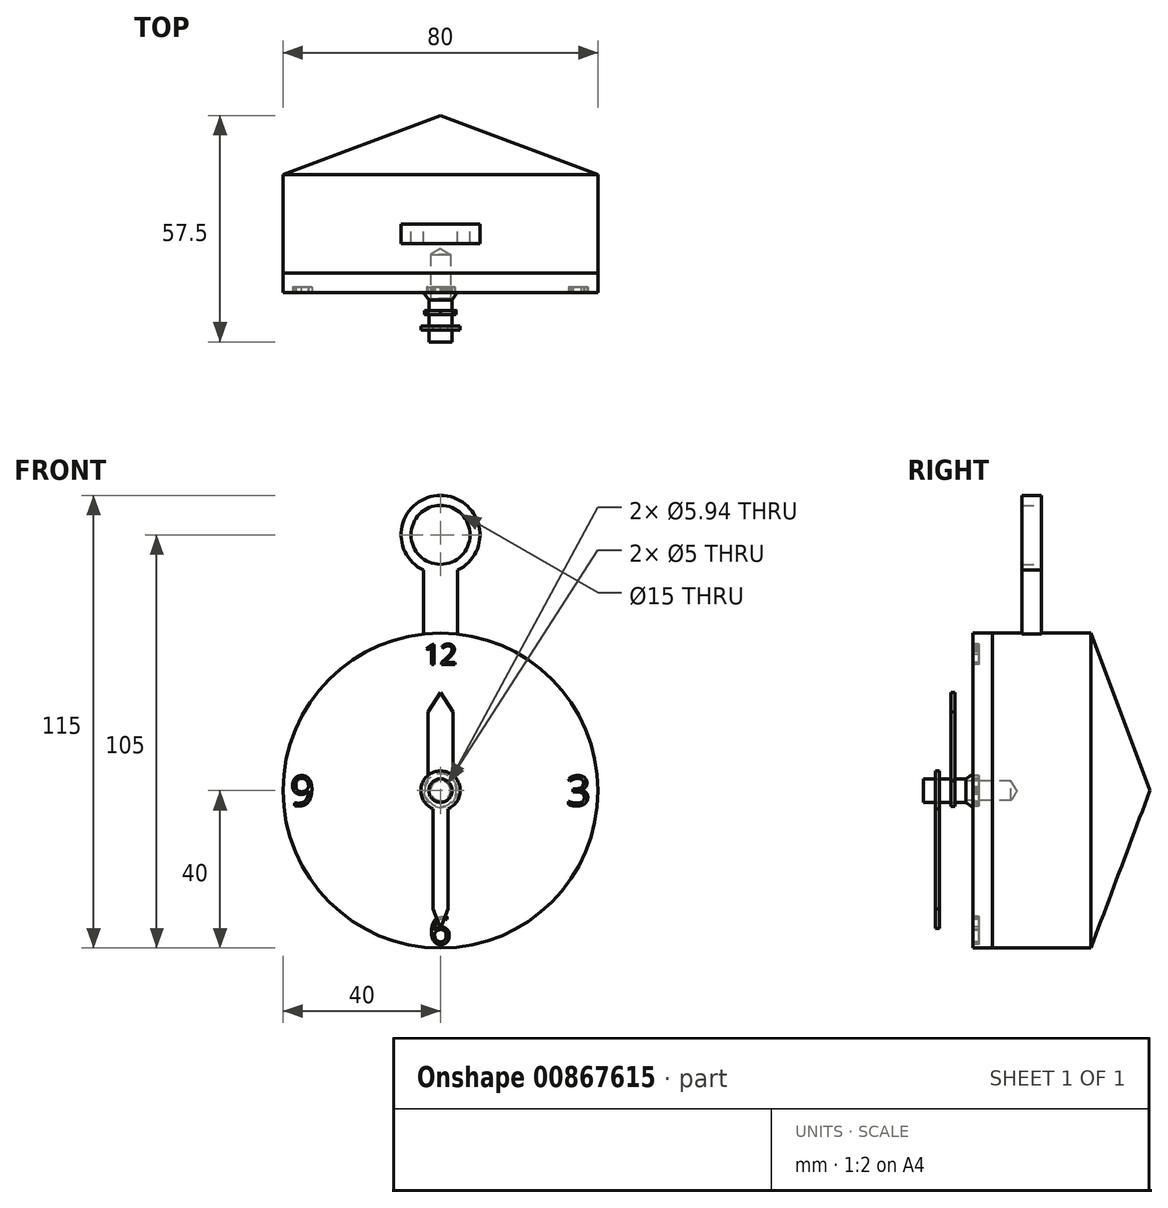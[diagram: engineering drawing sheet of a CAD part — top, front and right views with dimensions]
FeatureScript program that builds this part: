
annotation { "Feature Type Name" : "Feature", "Feature Type Description" : "" }
export const myFeature = defineFeature(function(context is Context, id is Id, definition is map)
    precondition{}
    {
        {
            var Q0;
            Q0=qCreatedBy(makeId("Front.planeOp"),FACE);
            var sketch = newSketch(context, id + "F0", { "sketchPlane" : qUnion([Q0])});
            skCircle(sketch, "E0", {"center": v(0, 0) * mm, "radius": 40 * mm});
            skSolve(sketch);
        }
        {
            var Q0;
            Q0=makeQuery(id+"F0.imprint","IMPRINT",FACE,{"disambiguationData":[TD([[makeQuery(id+"F0.imprint","IMPRINT",EDGE,{"derivedFrom":sQuery(id+"F0.wireOp",EDGE,"E0")}),1.0]])]});
            extrude(context, id + "F1", {"entities" : qUnion([Q0]), "endBound" : BoundingType.SYMMETRIC, "depth" : 25 * mm, "offsetDistance" : 25 * mm});
        }
        {
            var Q0;
            Q0=makeQuery(id+"F1.opExtrude","CAP_FACE",FACE,{"disambiguationData":[OSD([sQuery(id+"F0.wireOp",EDGE,"E0")])],"isStart":true});
            var sketch = newSketch(context, id + "F2", { "sketchPlane" : qUnion([Q0])});
            skSolve(sketch);
        }
        {
            var Q0;
            Q0=makeQuery(id+"F2.imprint","IMPRINT",FACE,{"disambiguationData":[TD([[makeQuery(id+"F2.imprint","IMPRINT",EDGE,{"derivedFrom":makeQuery(id+"F1.opExtrude","CAP_EDGE",EDGE,{"disambiguationData":[OSD([sQuery(id+"F0.wireOp",EDGE,"E0")])],"isStart":true})}),-1.0]])]});
            cPlane(context, id + "F3", {"entities" : qUnion([Q0]), "cplaneType" : CPlaneType.OFFSET, "offset" : 15 * mm, "width" : 150 * mm, "height" : 150 * mm});
        }
        {
            var Q0;
            Q0=qCreatedBy(id+"F3.planeOp",FACE);
            var sketch = newSketch(context, id + "F4", { "sketchPlane" : qUnion([Q0])});
            skPoint(sketch, "E1", {"position": v(0, 0) * mm});
            skSolve(sketch);
        }
        {
            var Q0;
            Q0=sQuery(id+"FzRARXqQxgSWfqW_1.wireOp",EDGE,"R4HBZe7h-dPAi-faUW-LI31-kF577Gu9LWN3");
            var Q1;
            Q1=sQuery(id+"FHscHiDwKJqEqJl_1.wireOp",EDGE,"caf13c96-3b14-45e5-a936-a351d3d8df380.MirrorCS");
            var Q2;
            Q2=sQuery(id+"FzRARXqQxgSWfqW_1.wireOp",EDGE,"7aed7209-74bc-49f3-b477-968225ddfcb50.MirrorCS");
            var Q3;
            Q3=sQuery(id+"FHscHiDwKJqEqJl_1.wireOp",EDGE,"4JvzB8gR-oUBM-6mn4-xHmX-QHIRwTSJfbtS");
            var Q5;
            Q5=makeQuery(id+"F2.imprint","IMPRINT",FACE,{"disambiguationData":[TD([[makeQuery(id+"F2.imprint","IMPRINT",EDGE,{"derivedFrom":makeQuery(id+"F1.opExtrude","CAP_EDGE",EDGE,{"disambiguationData":[OSD([sQuery(id+"F0.wireOp",EDGE,"E0")])],"isStart":true})}),-1.0]])]});
            var Q6;
            Q6=sQuery(id+"F4.wireOp",VERTEX,"E1");
            var Q7;
            Q7=sQuery(id+"FzRARXqQxgSWfqW_1.wireOp",EDGE,"R4HBZe7h-dPAi-faUW-LI31-kF577Gu9LWN3");
            var Q8;
            Q8=sQuery(id+"FHscHiDwKJqEqJl_1.wireOp",EDGE,"caf13c96-3b14-45e5-a936-a351d3d8df380.MirrorCS");
            var Q9;
            Q9=sQuery(id+"FzRARXqQxgSWfqW_1.wireOp",EDGE,"7aed7209-74bc-49f3-b477-968225ddfcb50.MirrorCS");
            var Q10;
            Q10=sQuery(id+"FHscHiDwKJqEqJl_1.wireOp",EDGE,"4JvzB8gR-oUBM-6mn4-xHmX-QHIRwTSJfbtS");
            loft(context, id + "F5", {"operationType" : NewBodyOperationType.ADD, "spine" : qUnion([Q0, Q1, Q2, Q3]), "sheetProfilesArray" : [{ "sheetProfileEntities" : qUnion([Q5]) }, { "sheetProfileEntities" : qUnion([Q6]) }], "guidesArray" : [{ "guideEntities" : qUnion([Q7]), "guideDerivativeType" : LoftGuideDerivativeType.DEFAULT, "guideDerivativeMagnitude" : 1 }, { "guideEntities" : qUnion([Q8]), "guideDerivativeType" : LoftGuideDerivativeType.DEFAULT, "guideDerivativeMagnitude" : 1 }, { "guideEntities" : qUnion([Q9]), "guideDerivativeType" : LoftGuideDerivativeType.DEFAULT, "guideDerivativeMagnitude" : 1 }, { "guideEntities" : qUnion([Q10]), "guideDerivativeType" : LoftGuideDerivativeType.DEFAULT, "guideDerivativeMagnitude" : 1 }]});
        }
        {
            var Q0;
            Q0=makeQuery(id+"F1.opExtrude","CAP_FACE",FACE,{"disambiguationData":[OSD([sQuery(id+"F0.wireOp",EDGE,"E0")])],"isStart":false});
            var sketch = newSketch(context, id + "F6", { "sketchPlane" : qUnion([Q0])});
            skCircle(sketch, "E2", {"center": v(0, 0) * mm, "radius": 40 * mm});
            skSolve(sketch);
        }
        {
            var Q0;
            Q0 = qSketchRegion(id + "F6", true);
            extrude(context, id + "F7", {"entities" : qUnion([Q0]), "depth" : 5 * mm, "offsetDistance" : 25 * mm});
        }
        {
            var Q0;
            Q0=makeQuery(id+"F7.opExtrude","CAP_FACE",FACE,{"disambiguationData":[OSD([sQuery(id+"F6.wireOp",EDGE,"E2")])],"isStart":false});
            var sketch = newSketch(context, id + "F8", { "sketchPlane" : qUnion([Q0])});
            skCircle(sketch, "E3", {"center": v(0, 0) * mm, "radius": 4.25 * mm});
            skSolve(sketch);
        }
        {
            var Q0;
            Q0=makeQuery(id+"F8.imprint","IMPRINT",FACE,{"disambiguationData":[TD([[makeQuery(id+"F8.imprint","IMPRINT",EDGE,{"derivedFrom":sQuery(id+"F8.wireOp",EDGE,"E3")}),-1.0]])]});
            cPlane(context, id + "F9", {"entities" : qUnion([Q0]), "cplaneType" : CPlaneType.OFFSET, "offset" : 2.25 * mm, "width" : 150 * mm, "height" : 150 * mm});
        }
        {
            var Q0;
            Q0=qCreatedBy(id+"F9.planeOp",FACE);
            var sketch = newSketch(context, id + "F10", { "sketchPlane" : qUnion([Q0])});
            skCircle(sketch, "E4.0", {"center": v(0, 0) * mm, "radius": 2.65 * mm});
            skSolve(sketch);
        }
        {
            var Q1;
            Q1=makeQuery(id+"F8.imprint","IMPRINT",FACE,{"disambiguationData":[TD([[makeQuery(id+"F8.imprint","IMPRINT",EDGE,{"derivedFrom":sQuery(id+"F8.wireOp",EDGE,"E3")}),1.0]])]});
            var Q2;
            Q2=makeQuery(id+"F10.imprint","IMPRINT",FACE,{"disambiguationData":[TD([[makeQuery(id+"F10.imprint","IMPRINT",EDGE,{"derivedFrom":sQuery(id+"F10.wireOp",EDGE,"E4.0")}),1.0]])]});
            loft(context, id + "F11", {"operationType" : NewBodyOperationType.ADD, "sheetProfilesArray" : [{ "sheetProfileEntities" : qUnion([Q1]) }, { "sheetProfileEntities" : qUnion([Q2]) }]});
        }
        {
            var Q0;
            Q0=qCreatedBy(id+"F9.planeOp",FACE);
            cPlane(context, id + "F12", {"entities" : qUnion([Q0]), "cplaneType" : CPlaneType.OFFSET, "offset" : 0 * mm, "width" : 150 * mm, "height" : 150 * mm});
        }
        {
            var Q0;
            Q0=qCreatedBy(id+"F12.planeOp",FACE);
            var sketch = newSketch(context, id + "F13", { "sketchPlane" : qUnion([Q0])});
            skPoint(sketch, "E5", {"position": v(0, 0) * mm});
            skSolve(sketch);
        }
        {
            var Q0;
            Q0=sQuery(id+"F13.wireOp",VERTEX,"E5");
            var Q1;
            Q1=makeQuery(id+"F1.opExtrude","SWEPT_BODY",BODY,{"disambiguationData":[OSD([sQuery(id+"F0.wireOp",EDGE,"E0")])]});
            var Q2;
            Q2=makeQuery(id+"F7.opExtrude","SWEPT_BODY",BODY,{"disambiguationData":[OSD([sQuery(id+"F6.wireOp",EDGE,"E2")])]});
            var Q3;
            Q3=makeQuery(id+"F11.opLoft","SWEPT_BODY",BODY,{"disambiguationData":[OSD([makeQuery(id+"F8.imprint","IMPRINT",FACE,{"disambiguationData":[TD([[makeQuery(id+"F8.imprint","IMPRINT",EDGE,{"derivedFrom":sQuery(id+"F8.wireOp",EDGE,"E3")}),1.0]])]}),makeQuery(id+"F10.imprint","IMPRINT",FACE,{"disambiguationData":[TD([[makeQuery(id+"F10.imprint","IMPRINT",EDGE,{"derivedFrom":sQuery(id+"F10.wireOp",EDGE,"E4.0")}),1.0]])]})])]});
            hole(context, id + "F14", {"style" : HoleStyle.C_SINK, "endStyle" : HoleEndStyle.BLIND, "holeDiameter" : 5 * mm, "cSinkDiameter" : 7.5 * mm, "cSinkAngle" : 120 * degree, "majorDiameter" : 5 * mm, "holeDepth" : 12 * mm, "isTappedThrough" : true, "tappedDepth" : 12 * mm, "tapClearance" : 3, "startFromSketch" : true, "locations" : qUnion([Q0]), "scope" : qUnion([Q1, Q2, Q3])});
        }
        {
            var Q0;
            Q0=makeQuery(id+"F7.opExtrude","CAP_FACE",FACE,{"disambiguationData":[OSD([sQuery(id+"F6.wireOp",EDGE,"E2")])],"isStart":false});
            var sketch = newSketch(context, id + "F15", { "sketchPlane" : qUnion([Q0])});
            skCircle(sketch, "E6.0", {"center": v(0, 0) * mm, "radius": 2.97 * mm});
            skSolve(sketch);
        }
        {
            var Q0;
            Q0 = qSketchRegion(id + "F15", true);
            extrude(context, id + "F16", {"entities" : qUnion([Q0]), "endBound" : BoundingType.SYMMETRIC, "depth" : 25 * mm, "offsetDistance" : 25 * mm});
        }
        {
            var Q0;
            Q0=makeQuery(id+"F7.opExtrude","SWEPT_BODY",BODY,{"disambiguationData":[OSD([sQuery(id+"F6.wireOp",EDGE,"E2")])]});
            var Q1;
            Q1=makeQuery(id+"F1.opExtrude","SWEPT_BODY",BODY,{"disambiguationData":[OSD([sQuery(id+"F0.wireOp",EDGE,"E0")])]});
            var Q2;
            Q2=makeQuery(id+"F11.opLoft","SWEPT_BODY",BODY,{"disambiguationData":[OSD([makeQuery(id+"F8.imprint","IMPRINT",FACE,{"disambiguationData":[TD([[makeQuery(id+"F8.imprint","IMPRINT",EDGE,{"derivedFrom":sQuery(id+"F8.wireOp",EDGE,"E3")}),1.0]])]}),makeQuery(id+"F10.imprint","IMPRINT",FACE,{"disambiguationData":[TD([[makeQuery(id+"F10.imprint","IMPRINT",EDGE,{"derivedFrom":sQuery(id+"F10.wireOp",EDGE,"E4.0")}),1.0]])]})])]});
            var Q3;
            Q3=makeQuery(id+"F16.opExtrude","SWEPT_BODY",BODY,{"disambiguationData":[OSD([sQuery(id+"F15.wireOp",EDGE,"E6.0")])]});
            booleanBodies(context, id + "F17", {"operationType" : BooleanOperationType.SUBTRACTION, "tools" : qUnion([Q0, Q1, Q2]), "targets" : qUnion([Q3]), "keepTools" : true});
        }
        {
            var Q0;
            Q0=makeQuery(id+"F7.opExtrude","CAP_FACE",FACE,{"disambiguationData":[OSD([sQuery(id+"F6.wireOp",EDGE,"E2")])],"isStart":false});
            var sketch = newSketch(context, id + "F18", { "sketchPlane" : qUnion([Q0])});
            skText(sketch, "E7", { "text": "12", "fontName": "OpenSans-Regular.ttf"});
            skText(sketch, "E8", { "text": "3", "fontName": "OpenSans-Regular.ttf"});
            skText(sketch, "E9", { "text": "6", "fontName": "OpenSans-Regular.ttf"});
            skText(sketch, "E10", { "text": "9", "fontName": "OpenSans-Regular.ttf"});
            const initialGuessF18  = {"E7": [-0.0042, 0.032, 1, 0, 0.00524], "E8": [0.032, -0.0038, 1, 0, 0.0076], "E9": [-0.00286, -0.039, 1, 0, 0.007], "E10": [-0.03815, -0.0038, 1, 0, 0.0076]};
            skSetInitialGuess(sketch, initialGuessF18);
            skSolve(sketch);
        }
        {
            var Q0;
            Q0 = qSketchRegion(id + "F18", true);
            extrude(context, id + "F19", {"entities" : qUnion([Q0]), "oppositeDirection" : true, "depth" : 1.5 * mm, "offsetDistance" : 25 * mm});
        }
        {
            var Q0;
            Q0=makeQuery(id+"F19.opExtrude","SWEPT_BODY",BODY,{"disambiguationData":[OSD([sQuery(id+"F18.wireOp",EDGE,"E10.sketch_text.stroke-0"),sQuery(id+"F18.wireOp",EDGE,"E10.sketch_text.stroke-1"),sQuery(id+"F18.wireOp",EDGE,"E10.sketch_text.stroke-2"),sQuery(id+"F18.wireOp",EDGE,"E10.sketch_text.stroke-3"),sQuery(id+"F18.wireOp",EDGE,"E10.sketch_text.stroke-4"),sQuery(id+"F18.wireOp",EDGE,"E10.sketch_text.stroke-5"),sQuery(id+"F18.wireOp",EDGE,"E10.sketch_text.stroke-6"),sQuery(id+"F18.wireOp",EDGE,"E10.sketch_text.stroke-7"),sQuery(id+"F18.wireOp",EDGE,"E10.sketch_text.stroke-8"),sQuery(id+"F18.wireOp",EDGE,"E10.sketch_text.stroke-9"),sQuery(id+"F18.wireOp",EDGE,"E10.sketch_text.stroke-10"),sQuery(id+"F18.wireOp",EDGE,"E10.sketch_text.stroke-11"),sQuery(id+"F18.wireOp",EDGE,"E10.sketch_text.stroke-12"),sQuery(id+"F18.wireOp",EDGE,"E10.sketch_text.stroke-13"),sQuery(id+"F18.wireOp",EDGE,"E10.sketch_text.stroke-14"),sQuery(id+"F18.wireOp",EDGE,"E10.sketch_text.stroke-15"),sQuery(id+"F18.wireOp",EDGE,"E10.sketch_text.stroke-16"),sQuery(id+"F18.wireOp",EDGE,"E10.sketch_text.stroke-17"),sQuery(id+"F18.wireOp",EDGE,"E10.sketch_text.stroke-18"),sQuery(id+"F18.wireOp",EDGE,"E10.sketch_text.stroke-19"),sQuery(id+"F18.wireOp",EDGE,"E10.sketch_text.stroke-20"),sQuery(id+"F18.wireOp",EDGE,"E10.sketch_text.stroke-21"),sQuery(id+"F18.wireOp",EDGE,"E10.sketch_text.stroke-22"),sQuery(id+"F18.wireOp",EDGE,"E10.sketch_text.stroke-23"),sQuery(id+"F18.wireOp",EDGE,"E10.sketch_text.stroke-24"),sQuery(id+"F18.wireOp",EDGE,"E10.sketch_text.stroke-25")])]});
            var Q1;
            Q1=makeQuery(id+"F19.opExtrude","SWEPT_BODY",BODY,{"disambiguationData":[OSD([sQuery(id+"F18.wireOp",EDGE,"E7.sketch_text.stroke-0"),sQuery(id+"F18.wireOp",EDGE,"E7.sketch_text.stroke-1"),sQuery(id+"F18.wireOp",EDGE,"E7.sketch_text.stroke-2"),sQuery(id+"F18.wireOp",EDGE,"E7.sketch_text.stroke-3"),sQuery(id+"F18.wireOp",EDGE,"E7.sketch_text.stroke-4"),sQuery(id+"F18.wireOp",EDGE,"E7.sketch_text.stroke-5"),sQuery(id+"F18.wireOp",EDGE,"E7.sketch_text.stroke-6"),sQuery(id+"F18.wireOp",EDGE,"E7.sketch_text.stroke-7"),sQuery(id+"F18.wireOp",EDGE,"E7.sketch_text.stroke-8")])]});
            var Q2;
            Q2=makeQuery(id+"F19.opExtrude","SWEPT_BODY",BODY,{"disambiguationData":[OSD([sQuery(id+"F18.wireOp",EDGE,"E7.sketch_text.stroke-9"),sQuery(id+"F18.wireOp",EDGE,"E7.sketch_text.stroke-10"),sQuery(id+"F18.wireOp",EDGE,"E7.sketch_text.stroke-11"),sQuery(id+"F18.wireOp",EDGE,"E7.sketch_text.stroke-12"),sQuery(id+"F18.wireOp",EDGE,"E7.sketch_text.stroke-13"),sQuery(id+"F18.wireOp",EDGE,"E7.sketch_text.stroke-14"),sQuery(id+"F18.wireOp",EDGE,"E7.sketch_text.stroke-15"),sQuery(id+"F18.wireOp",EDGE,"E7.sketch_text.stroke-16"),sQuery(id+"F18.wireOp",EDGE,"E7.sketch_text.stroke-17"),sQuery(id+"F18.wireOp",EDGE,"E7.sketch_text.stroke-18"),sQuery(id+"F18.wireOp",EDGE,"E7.sketch_text.stroke-19"),sQuery(id+"F18.wireOp",EDGE,"E7.sketch_text.stroke-20"),sQuery(id+"F18.wireOp",EDGE,"E7.sketch_text.stroke-21"),sQuery(id+"F18.wireOp",EDGE,"E7.sketch_text.stroke-22"),sQuery(id+"F18.wireOp",EDGE,"E7.sketch_text.stroke-23"),sQuery(id+"F18.wireOp",EDGE,"E7.sketch_text.stroke-24"),sQuery(id+"F18.wireOp",EDGE,"E7.sketch_text.stroke-25"),sQuery(id+"F18.wireOp",EDGE,"E7.sketch_text.stroke-26"),sQuery(id+"F18.wireOp",EDGE,"E7.sketch_text.stroke-27"),sQuery(id+"F18.wireOp",EDGE,"E7.sketch_text.stroke-28")])]});
            var Q3;
            Q3=makeQuery(id+"F19.opExtrude","SWEPT_BODY",BODY,{"disambiguationData":[OSD([sQuery(id+"F18.wireOp",EDGE,"E8.sketch_text.stroke-0"),sQuery(id+"F18.wireOp",EDGE,"E8.sketch_text.stroke-1"),sQuery(id+"F18.wireOp",EDGE,"E8.sketch_text.stroke-2"),sQuery(id+"F18.wireOp",EDGE,"E8.sketch_text.stroke-3"),sQuery(id+"F18.wireOp",EDGE,"E8.sketch_text.stroke-4"),sQuery(id+"F18.wireOp",EDGE,"E8.sketch_text.stroke-5"),sQuery(id+"F18.wireOp",EDGE,"E8.sketch_text.stroke-6"),sQuery(id+"F18.wireOp",EDGE,"E8.sketch_text.stroke-7"),sQuery(id+"F18.wireOp",EDGE,"E8.sketch_text.stroke-8"),sQuery(id+"F18.wireOp",EDGE,"E8.sketch_text.stroke-9"),sQuery(id+"F18.wireOp",EDGE,"E8.sketch_text.stroke-10"),sQuery(id+"F18.wireOp",EDGE,"E8.sketch_text.stroke-11"),sQuery(id+"F18.wireOp",EDGE,"E8.sketch_text.stroke-12"),sQuery(id+"F18.wireOp",EDGE,"E8.sketch_text.stroke-13"),sQuery(id+"F18.wireOp",EDGE,"E8.sketch_text.stroke-14"),sQuery(id+"F18.wireOp",EDGE,"E8.sketch_text.stroke-15"),sQuery(id+"F18.wireOp",EDGE,"E8.sketch_text.stroke-16"),sQuery(id+"F18.wireOp",EDGE,"E8.sketch_text.stroke-17"),sQuery(id+"F18.wireOp",EDGE,"E8.sketch_text.stroke-18"),sQuery(id+"F18.wireOp",EDGE,"E8.sketch_text.stroke-19"),sQuery(id+"F18.wireOp",EDGE,"E8.sketch_text.stroke-20"),sQuery(id+"F18.wireOp",EDGE,"E8.sketch_text.stroke-21"),sQuery(id+"F18.wireOp",EDGE,"E8.sketch_text.stroke-22"),sQuery(id+"F18.wireOp",EDGE,"E8.sketch_text.stroke-23"),sQuery(id+"F18.wireOp",EDGE,"E8.sketch_text.stroke-24"),sQuery(id+"F18.wireOp",EDGE,"E8.sketch_text.stroke-25"),sQuery(id+"F18.wireOp",EDGE,"E8.sketch_text.stroke-26"),sQuery(id+"F18.wireOp",EDGE,"E8.sketch_text.stroke-27")])]});
            var Q4;
            Q4=makeQuery(id+"F19.opExtrude","SWEPT_BODY",BODY,{"disambiguationData":[OSD([sQuery(id+"F18.wireOp",EDGE,"E9.sketch_text.stroke-0"),sQuery(id+"F18.wireOp",EDGE,"E9.sketch_text.stroke-1"),sQuery(id+"F18.wireOp",EDGE,"E9.sketch_text.stroke-2"),sQuery(id+"F18.wireOp",EDGE,"E9.sketch_text.stroke-3"),sQuery(id+"F18.wireOp",EDGE,"E9.sketch_text.stroke-4"),sQuery(id+"F18.wireOp",EDGE,"E9.sketch_text.stroke-5"),sQuery(id+"F18.wireOp",EDGE,"E9.sketch_text.stroke-6"),sQuery(id+"F18.wireOp",EDGE,"E9.sketch_text.stroke-7"),sQuery(id+"F18.wireOp",EDGE,"E9.sketch_text.stroke-8"),sQuery(id+"F18.wireOp",EDGE,"E9.sketch_text.stroke-9"),sQuery(id+"F18.wireOp",EDGE,"E9.sketch_text.stroke-10"),sQuery(id+"F18.wireOp",EDGE,"E9.sketch_text.stroke-11"),sQuery(id+"F18.wireOp",EDGE,"E9.sketch_text.stroke-12"),sQuery(id+"F18.wireOp",EDGE,"E9.sketch_text.stroke-13"),sQuery(id+"F18.wireOp",EDGE,"E9.sketch_text.stroke-14"),sQuery(id+"F18.wireOp",EDGE,"E9.sketch_text.stroke-15"),sQuery(id+"F18.wireOp",EDGE,"E9.sketch_text.stroke-16"),sQuery(id+"F18.wireOp",EDGE,"E9.sketch_text.stroke-17"),sQuery(id+"F18.wireOp",EDGE,"E9.sketch_text.stroke-18"),sQuery(id+"F18.wireOp",EDGE,"E9.sketch_text.stroke-19"),sQuery(id+"F18.wireOp",EDGE,"E9.sketch_text.stroke-20"),sQuery(id+"F18.wireOp",EDGE,"E9.sketch_text.stroke-21"),sQuery(id+"F18.wireOp",EDGE,"E9.sketch_text.stroke-22"),sQuery(id+"F18.wireOp",EDGE,"E9.sketch_text.stroke-23"),sQuery(id+"F18.wireOp",EDGE,"E9.sketch_text.stroke-24")])]});
            var Q5;
            Q5=makeQuery(id+"F7.opExtrude","SWEPT_BODY",BODY,{"disambiguationData":[OSD([sQuery(id+"F6.wireOp",EDGE,"E2")])]});
            booleanBodies(context, id + "F20", {"operationType" : BooleanOperationType.SUBTRACTION, "tools" : qUnion([Q0, Q1, Q2, Q3, Q4]), "targets" : qUnion([Q5])});
        }
        {
            var Q0;
            Q0=qCreatedBy(makeId("Front.planeOp"),FACE);
            var sketch = newSketch(context, id + "F21", { "sketchPlane" : qUnion([Q0])});
            skArc(sketch, "E11", {"start": v(4.36, 56) * mm, "mid": v(0, 75) * mm, "end": v(-4.36, 56) * mm});
            skLineSegment(sketch, "E12", {"start": v(-4.36, 56) * mm, "end": v(-4.36, 30) * mm});
            skLineSegment(sketch, "E13", {"start": v(-4.36, 30) * mm, "end": v(4.34, 30) * mm});
            skLineSegment(sketch, "E14", {"start": v(4.34, 30) * mm, "end": v(4.36, 56) * mm});
            skSolve(sketch);
        }
        {
            var Q0;
            Q0 = qSketchRegion(id + "F21", true);
            extrude(context, id + "F22", {"entities" : qUnion([Q0]), "operationType" : NewBodyOperationType.ADD, "depth" : 5 * mm, "offsetDistance" : 25 * mm});
        }
        {
            var Q0;
            Q0=makeQuery(id+"F22.opExtrude","CAP_FACE",FACE,{"disambiguationData":[OSD([sQuery(id+"F21.wireOp",EDGE,"E11"),sQuery(id+"F21.wireOp",EDGE,"E12"),sQuery(id+"F21.wireOp",EDGE,"E13"),sQuery(id+"F21.wireOp",EDGE,"E14")])],"isStart":false});
            var sketch = newSketch(context, id + "F23", { "sketchPlane" : qUnion([Q0])});
            skCircle(sketch, "E15", {"center": v(0, 65) * mm, "radius": 7.5 * mm});
            skSolve(sketch);
        }
        {
            var Q0;
            Q0 = qSketchRegion(id + "F23", true);
            extrude(context, id + "F24", {"entities" : qUnion([Q0]), "operationType" : NewBodyOperationType.REMOVE, "endBound" : BoundingType.SYMMETRIC, "depth" : 25 * mm, "offsetDistance" : 25 * mm});
        }
        {
            var Q0;
            {var subQ0=sQuery(id+"F6.wireOp",EDGE,"E2");Q0=makeQuery(id+"F20.opBoolean","SPLIT",FACE,{"disambiguationData":[TD([makeQuery(id+"F7.opExtrude","SWEPT_FACE",FACE,{"disambiguationData":[OSD([subQ0])]})])],"derivedFrom":makeQuery(id+"F7.opExtrude","CAP_FACE",FACE,{"disambiguationData":[OSD([subQ0])],"isStart":false})});}
            cPlane(context, id + "F25", {"entities" : qUnion([Q0]), "cplaneType" : CPlaneType.OFFSET, "offset" : 4.5 * mm, "width" : 150 * mm, "height" : 150 * mm});
        }
        {
            var Q0;
            Q0=qCreatedBy(id+"F25.planeOp",FACE);
            var sketch = newSketch(context, id + "F26", { "sketchPlane" : qUnion([Q0])});
            skArc(sketch, "E16", {"start": v(-3.12, 2.5) * mm, "mid": v(0, -4) * mm, "end": v(3.12, 2.5) * mm});
            skLineSegment(sketch, "E17", {"start": v(-3.12, 2.5) * mm, "end": v(-3.12, 20) * mm});
            skLineSegment(sketch, "E18", {"start": v(-3.12, 20) * mm, "end": v(0, 25) * mm});
            skLineSegment(sketch, "E19", {"start": v(0, 25) * mm, "end": v(3.12, 20) * mm});
            skLineSegment(sketch, "E20", {"start": v(3.12, 20) * mm, "end": v(3.12, 2.5) * mm});
            skSolve(sketch);
        }
        {
            var Q0;
            Q0 = qSketchRegion(id + "F26", true);
            extrude(context, id + "F27", {"entities" : qUnion([Q0]), "depth" : 1 * mm, "offsetDistance" : 25 * mm});
        }
        {
            var Q0;
            Q0=makeQuery(id+"F1.opExtrude","SWEPT_BODY",BODY,{"disambiguationData":[OSD([sQuery(id+"F0.wireOp",EDGE,"E0")])]});
            var Q1;
            Q1=makeQuery(id+"F27.opExtrude","SWEPT_BODY",BODY,{"disambiguationData":[OSD([sQuery(id+"F26.wireOp",EDGE,"E16"),sQuery(id+"F26.wireOp",EDGE,"E17"),sQuery(id+"F26.wireOp",EDGE,"E18"),sQuery(id+"F26.wireOp",EDGE,"E19"),sQuery(id+"F26.wireOp",EDGE,"E20")])]});
            booleanBodies(context, id + "F28", {"operationType" : BooleanOperationType.SUBTRACTION, "tools" : qUnion([Q0]), "targets" : qUnion([Q1]), "keepTools" : true});
        }
        {
            var Q0;
            {var subQ0=sQuery(id+"F6.wireOp",EDGE,"E2");Q0=makeQuery(id+"F20.opBoolean","SPLIT",FACE,{"disambiguationData":[TD([makeQuery(id+"F7.opExtrude","SWEPT_FACE",FACE,{"disambiguationData":[OSD([subQ0])]})])],"derivedFrom":makeQuery(id+"F7.opExtrude","CAP_FACE",FACE,{"disambiguationData":[OSD([subQ0])],"isStart":false})});}
            cPlane(context, id + "F29", {"entities" : qUnion([Q0]), "cplaneType" : CPlaneType.OFFSET, "offset" : 8.5 * mm, "width" : 150 * mm, "height" : 150 * mm});
        }
        {
            var Q0;
            Q0=qCreatedBy(id+"F29.planeOp",FACE);
            var sketch = newSketch(context, id + "F30", { "sketchPlane" : qUnion([Q0])});
            skArc(sketch, "E21", {"start": v(1.96, -4.6) * mm, "mid": v(0, 5) * mm, "end": v(-1.96, -4.6) * mm});
            skLineSegment(sketch, "E22", {"start": v(-1.96, -4.6) * mm, "end": v(-1.96, -30) * mm});
            skLineSegment(sketch, "E23", {"start": v(-1.96, -30) * mm, "end": v(0, -35) * mm});
            skLineSegment(sketch, "E24.MirrorCS", {"start": v(1.96, -4.6) * mm, "end": v(1.96, -30) * mm});
            skLineSegment(sketch, "E25.MirrorCS", {"start": v(1.96, -30) * mm, "end": v(0, -35) * mm});
            skSolve(sketch);
        }
        {
            var Q0;
            Q0 = qSketchRegion(id + "F30", true);
            extrude(context, id + "F31", {"entities" : qUnion([Q0]), "depth" : 1 * mm, "offsetDistance" : 25 * mm});
        }
        {
            var Q0;
            Q0=makeQuery(id+"F1.opExtrude","SWEPT_BODY",BODY,{"disambiguationData":[OSD([sQuery(id+"F0.wireOp",EDGE,"E0")])]});
            var Q1;
            Q1=makeQuery(id+"F31.opExtrude","SWEPT_BODY",BODY,{"disambiguationData":[OSD([sQuery(id+"F30.wireOp",EDGE,"E21"),sQuery(id+"F30.wireOp",EDGE,"E22"),sQuery(id+"F30.wireOp",EDGE,"E23"),sQuery(id+"F30.wireOp",EDGE,"E24.MirrorCS"),sQuery(id+"F30.wireOp",EDGE,"E25.MirrorCS")])]});
            booleanBodies(context, id + "F32", {"operationType" : BooleanOperationType.SUBTRACTION, "tools" : qUnion([Q0]), "targets" : qUnion([Q1]), "keepTools" : true});
        }
        {
            var Q0;
            Q0=makeQuery(id+"F16.opExtrude","SWEPT_BODY",BODY,{"disambiguationData":[OSD([sQuery(id+"F15.wireOp",EDGE,"E6.0")])]});
            var Q1;
            Q1=makeQuery(id+"F27.opExtrude","SWEPT_BODY",BODY,{"disambiguationData":[OSD([sQuery(id+"F26.wireOp",EDGE,"E16"),sQuery(id+"F26.wireOp",EDGE,"E17"),sQuery(id+"F26.wireOp",EDGE,"E18"),sQuery(id+"F26.wireOp",EDGE,"E19"),sQuery(id+"F26.wireOp",EDGE,"E20")])]});
            var Q2;
            Q2=makeQuery(id+"F31.opExtrude","SWEPT_BODY",BODY,{"disambiguationData":[OSD([sQuery(id+"F30.wireOp",EDGE,"E21"),sQuery(id+"F30.wireOp",EDGE,"E22"),sQuery(id+"F30.wireOp",EDGE,"E23"),sQuery(id+"F30.wireOp",EDGE,"E24.MirrorCS"),sQuery(id+"F30.wireOp",EDGE,"E25.MirrorCS")])]});
            booleanBodies(context, id + "F33", {"operationType" : BooleanOperationType.SUBTRACTION, "tools" : qUnion([Q0]), "targets" : qUnion([Q1, Q2]), "keepTools" : true});
        }
    });
